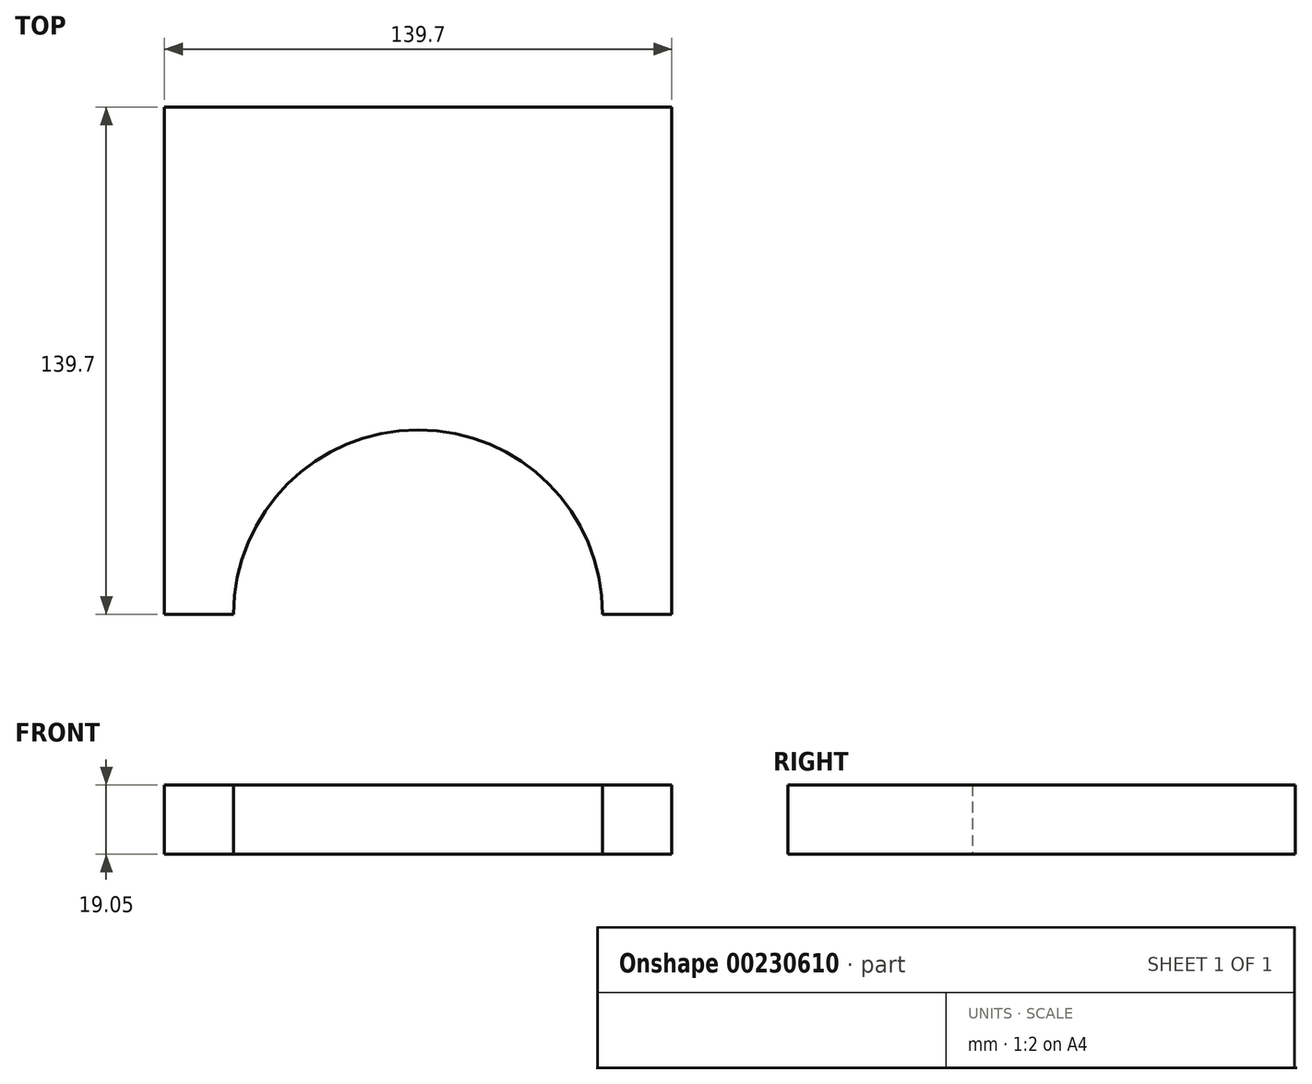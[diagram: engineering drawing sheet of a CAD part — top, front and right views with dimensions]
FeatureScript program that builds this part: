
annotation { "Feature Type Name" : "Feature", "Feature Type Description" : "" }
export const myFeature = defineFeature(function(context is Context, id is Id, definition is map)
    precondition{}
    {
        {
            var Q0;
            Q0=qCreatedBy(makeId("Top.planeOp"),FACE);
            var sketch = newSketch(context, id + "F0", { "sketchPlane" : qUnion([Q0])});
            skLineSegment(sketch, "E0.bottom", {"start": v(69.85, 70) * mm, "end": v(-69.85, 70) * mm});
            skLineSegment(sketch, "E0.top", {"start": v(69.85, -69.7) * mm, "end": v(50.8, -69.7) * mm});
            skLineSegment(sketch, "E0.left", {"start": v(69.85, 70) * mm, "end": v(69.85, -69.7) * mm});
            skLineSegment(sketch, "E0.right", {"start": v(-69.85, 70) * mm, "end": v(-69.85, -69.7) * mm});
            skPoint(sketch, "E0.middle", {"position": v(0, 0.14) * mm});
            skArc(sketch, "E1", {"start": v(50.8, -69.7) * mm, "mid": v(0, -18.9) * mm, "end": v(-50.8, -69.7) * mm});
            skLineSegment(sketch, "E2.trimOffspring", {"start": v(-50.8, -69.7) * mm, "end": v(-69.85, -69.7) * mm});
            skSolve(sketch);
        }
        {
            var Q0;
            Q0 = qSketchRegion(id + "F0", true);
            extrude(context, id + "F1", {"entities" : qUnion([Q0]), "depth" : 19.05 * mm});
        }
    });
